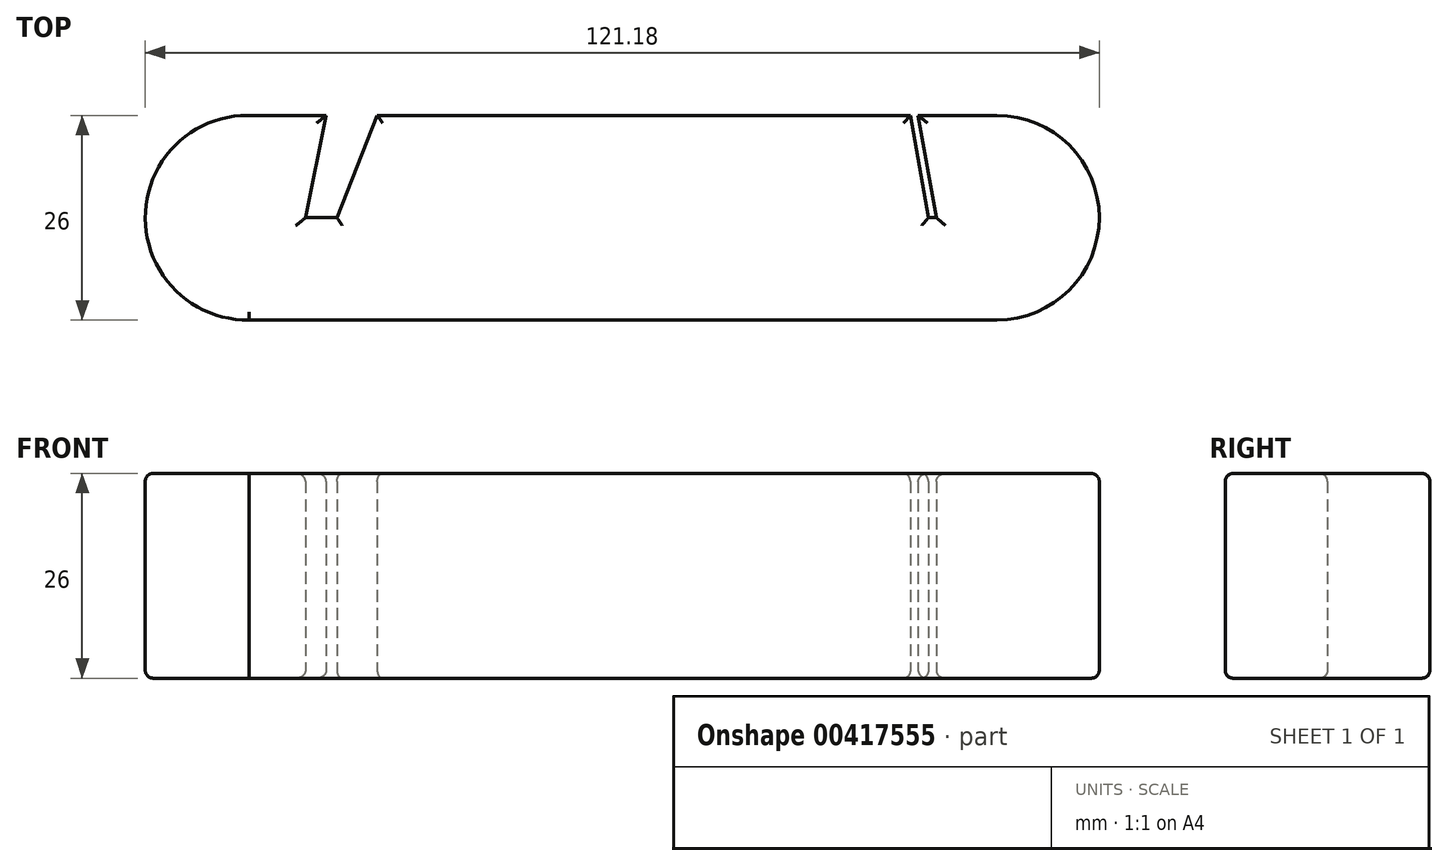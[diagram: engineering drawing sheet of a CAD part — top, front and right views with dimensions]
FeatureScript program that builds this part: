
annotation { "Feature Type Name" : "Feature", "Feature Type Description" : "" }
export const myFeature = defineFeature(function(context is Context, id is Id, definition is map)
    precondition{}
    {
        {
            var Q0;
            Q0=qCreatedBy(makeId("Top.planeOp"),FACE);
            var sketch = newSketch(context, id + "F0", { "sketchPlane" : qUnion([Q0])});
            skLineSegment(sketch, "E0", {"start": v(-46.17, 0) * mm, "end": v(48.83, 0) * mm});
            skLineSegment(sketch, "E1.0", {"start": v(-46.35, 26) * mm, "end": v(-36.35, 26) * mm});
            skArc(sketch, "E2", {"start": v(-46.35, 26) * mm, "mid": v(-59.35, 12.9) * mm, "end": v(-46.17, 0) * mm});
            skArc(sketch, "E3", {"start": v(48.83, 0) * mm, "mid": v(61.83, 13) * mm, "end": v(48.83, 26) * mm});
            skPoint(sketch, "E4", {"position": v(-36.35, 26) * mm});
            skPoint(sketch, "E5", {"position": v(-29.88, 26) * mm});
            skLineSegment(sketch, "E6.trimOffspring", {"start": v(-29.88, 26) * mm, "end": v(37.83, 26) * mm});
            skLineSegment(sketch, "E7", {"start": v(-36.35, 26) * mm, "end": v(-39, 13) * mm});
            skLineSegment(sketch, "E8", {"start": v(-29.88, 26) * mm, "end": v(-35, 13) * mm});
            skLineSegment(sketch, "E9", {"start": v(-35, 13) * mm, "end": v(-39, 13) * mm});
            skPoint(sketch, "E10", {"position": v(38.83, 26) * mm});
            skPoint(sketch, "E11", {"position": v(37.83, 26) * mm});
            skLineSegment(sketch, "E12.trimOffspring", {"start": v(38.83, 26) * mm, "end": v(48.83, 26) * mm});
            skLineSegment(sketch, "E13", {"start": v(37.83, 26) * mm, "end": v(40.12, 13) * mm});
            skLineSegment(sketch, "E14", {"start": v(40.12, 13) * mm, "end": v(41.12, 13) * mm});
            skLineSegment(sketch, "E15", {"start": v(41.12, 13) * mm, "end": v(38.83, 26) * mm});
            skSolve(sketch);
        }
        {
            var Q0;
            Q0=makeQuery(id+"F0.imprint","IMPRINT",FACE,{"disambiguationData":[TD([[makeQuery(id+"F0.imprint","IMPRINT",EDGE,{"derivedFrom":sQuery(id+"F0.wireOp",EDGE,"E0")}),1.0]])]});
            extrude(context, id + "F1", {"entities" : qUnion([Q0]), "depth" : 26 * mm});
        }
        {
            var Q0;
            Q0=makeQuery(id+"F1.opExtrude","CAP_FACE",FACE,{"disambiguationData":[OSD([sQuery(id+"F0.wireOp",EDGE,"E0"),sQuery(id+"F0.wireOp",EDGE,"E1.0"),sQuery(id+"F0.wireOp",EDGE,"E2"),sQuery(id+"F0.wireOp",EDGE,"E3"),sQuery(id+"F0.wireOp",EDGE,"E6.trimOffspring"),sQuery(id+"F0.wireOp",EDGE,"E7"),sQuery(id+"F0.wireOp",EDGE,"E8"),sQuery(id+"F0.wireOp",EDGE,"E9"),sQuery(id+"F0.wireOp",EDGE,"E12.trimOffspring"),sQuery(id+"F0.wireOp",EDGE,"E13"),sQuery(id+"F0.wireOp",EDGE,"E14"),sQuery(id+"F0.wireOp",EDGE,"E15")])],"isStart":false});
            var Q1;
            Q1=makeQuery(id+"F1.opExtrude","CAP_FACE",FACE,{"disambiguationData":[OSD([sQuery(id+"F0.wireOp",EDGE,"E0"),sQuery(id+"F0.wireOp",EDGE,"E1.0"),sQuery(id+"F0.wireOp",EDGE,"E2"),sQuery(id+"F0.wireOp",EDGE,"E3"),sQuery(id+"F0.wireOp",EDGE,"E6.trimOffspring"),sQuery(id+"F0.wireOp",EDGE,"E7"),sQuery(id+"F0.wireOp",EDGE,"E8"),sQuery(id+"F0.wireOp",EDGE,"E9"),sQuery(id+"F0.wireOp",EDGE,"E12.trimOffspring"),sQuery(id+"F0.wireOp",EDGE,"E13"),sQuery(id+"F0.wireOp",EDGE,"E14"),sQuery(id+"F0.wireOp",EDGE,"E15")])],"isStart":true});
            fillet(context, id + "F2", {"entities" : qUnion([Q0, Q1]), "radius" : 1 * mm, "tangentPropagation" : true, "allowEdgeOverflow" : false});
        }
    });
